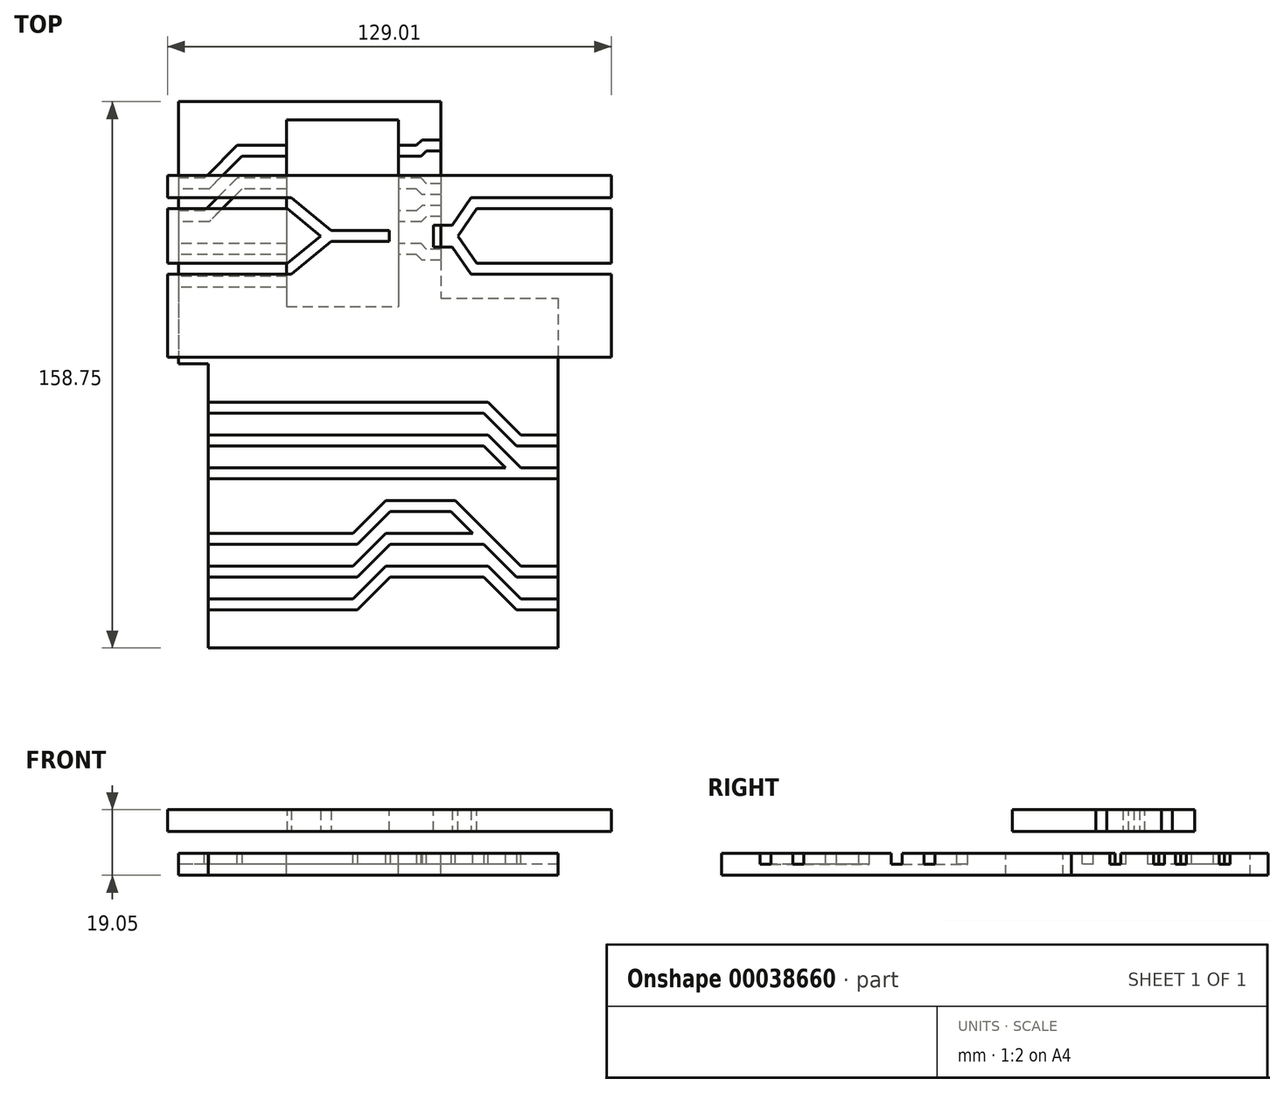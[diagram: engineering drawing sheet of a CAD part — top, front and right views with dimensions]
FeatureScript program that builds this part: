
annotation { "Feature Type Name" : "Feature", "Feature Type Description" : "" }
export const myFeature = defineFeature(function(context is Context, id is Id, definition is map)
    precondition{}
    {
        {
            var Q0;
            Q0=qCreatedBy(makeId("Top.planeOp"),FACE);
            var sketch = newSketch(context, id + "F0", { "sketchPlane" : qUnion([Q0])});
            skLineSegment(sketch, "E0.bottom", {"start": v(-61.1, 34.26) * mm, "end": v(40.5, 34.26) * mm});
            skLineSegment(sketch, "E0.top", {"start": v(-61.1, -67.34) * mm, "end": v(40.5, -67.34) * mm});
            skLineSegment(sketch, "E0.left", {"start": v(-61.1, 34.26) * mm, "end": v(-61.1, -67.34) * mm});
            skLineSegment(sketch, "E0.right", {"start": v(40.5, 34.26) * mm, "end": v(40.5, -67.34) * mm});
            skLineSegment(sketch, "E1.bottom", {"start": v(-69.8, 91.4) * mm, "end": v(6.4, 91.4) * mm});
            skLineSegment(sketch, "E1.top", {"start": v(-69.8, 15.2) * mm, "end": v(6.4, 15.2) * mm});
            skLineSegment(sketch, "E1.left", {"start": v(-69.8, 91.4) * mm, "end": v(-69.8, 15.2) * mm});
            skLineSegment(sketch, "E1.right", {"start": v(6.4, 91.4) * mm, "end": v(6.4, 15.2) * mm});
            skPoint(sketch, "E2", {"position": v(-61.1, 15.2) * mm});
            skPoint(sketch, "E3", {"position": v(6.4, 34.26) * mm});
            skSolve(sketch);
        }
        {
            var Q0;
            {var subQ1=sQuery(id+"F0.wireOp",EDGE,"E0.bottom");var subQ5=sQuery(id+"F0.wireOp",EDGE,"E0.left");var subQ7=makeQuery(id+"F0.imprint","INTERSECT",VERTEX,{"derivedFrom":[subQ1,subQ5]});Q0=makeQuery(id+"F0.imprint","IMPRINT",FACE,{"disambiguationData":[TD([[makeQuery(id+"F0.imprint","IMPRINT",EDGE,{"disambiguationData":[TD([[subQ7,-1.0]])],"derivedFrom":subQ1}),-1.0]])]});}
            var Q1;
            {var subQ8=sQuery(id+"F0.wireOp",EDGE,"E0.top");Q1=makeQuery(id+"F0.imprint","IMPRINT",FACE,{"disambiguationData":[TD([[makeQuery(id+"F0.imprint","IMPRINT",EDGE,{"derivedFrom":subQ8}),1.0]])]});}
            var Q2;
            {var subQ6=sQuery(id+"F0.wireOp",EDGE,"E1.bottom");Q2=makeQuery(id+"F0.imprint","IMPRINT",FACE,{"disambiguationData":[TD([[makeQuery(id+"F0.imprint","IMPRINT",EDGE,{"derivedFrom":subQ6}),-1.0]])]});}
            extrude(context, id + "F1", {"entities" : qUnion([Q0, Q1, Q2]), "oppositeDirection" : true, "depth" : 6.35 * mm});
        }
        {
            var Q0;
            Q0=makeQuery(id+"F1.opExtrude","CAP_FACE",FACE,{"disambiguationData":[OSD([sQuery(id+"F0.wireOp",EDGE,"E0.bottom"),sQuery(id+"F0.wireOp",EDGE,"E0.top"),sQuery(id+"F0.wireOp",EDGE,"E0.left"),sQuery(id+"F0.wireOp",EDGE,"E0.right"),sQuery(id+"F0.wireOp",EDGE,"E1.bottom"),sQuery(id+"F0.wireOp",EDGE,"E1.top"),sQuery(id+"F0.wireOp",EDGE,"E1.left"),sQuery(id+"F0.wireOp",EDGE,"E1.right")])],"isStart":true});
            var sketch = newSketch(context, id + "F2", { "sketchPlane" : qUnion([Q0])});
            skLineSegment(sketch, "E4", {"start": v(40.5, -7.02) * mm, "end": v(29.07, -7.02) * mm});
            skLineSegment(sketch, "E5", {"start": v(29.07, -7.02) * mm, "end": v(19.55, 2.5) * mm});
            skLineSegment(sketch, "E6", {"start": v(19.55, 2.5) * mm, "end": v(-61.1, 2.5) * mm});
            skLineSegment(sketch, "E7", {"start": v(40.5, -16.54) * mm, "end": v(29.07, -16.54) * mm});
            skLineSegment(sketch, "E8", {"start": v(29.07, -16.54) * mm, "end": v(19.55, -7.02) * mm});
            skLineSegment(sketch, "E9", {"start": v(19.55, -7.02) * mm, "end": v(-61.1, -7.02) * mm});
            skLineSegment(sketch, "E10", {"start": v(29.07, -16.54) * mm, "end": v(-61.1, -16.54) * mm});
            skLineSegment(sketch, "E11", {"start": v(40.5, -45.12) * mm, "end": v(29.07, -45.12) * mm});
            skLineSegment(sketch, "E12", {"start": v(29.07, -45.12) * mm, "end": v(19.55, -35.6) * mm});
            skLineSegment(sketch, "E13", {"start": v(10.02, -26.07) * mm, "end": v(-8.92, -26.07) * mm});
            skLineSegment(sketch, "E14", {"start": v(-8.92, -26.07) * mm, "end": v(-18.45, -35.6) * mm});
            skLineSegment(sketch, "E15", {"start": v(-18.45, -35.6) * mm, "end": v(-61.1, -35.6) * mm});
            skLineSegment(sketch, "E16", {"start": v(19.55, -35.6) * mm, "end": v(-8.92, -35.6) * mm});
            skLineSegment(sketch, "E17", {"start": v(-8.92, -35.6) * mm, "end": v(-18.45, -45.12) * mm});
            skLineSegment(sketch, "E18", {"start": v(-18.45, -45.12) * mm, "end": v(-61.1, -45.12) * mm});
            skLineSegment(sketch, "E19", {"start": v(40.5, -54.64) * mm, "end": v(29.07, -54.64) * mm});
            skLineSegment(sketch, "E20", {"start": v(29.07, -54.64) * mm, "end": v(19.55, -45.12) * mm});
            skLineSegment(sketch, "E21", {"start": v(19.55, -45.12) * mm, "end": v(-8.92, -45.12) * mm});
            skLineSegment(sketch, "E22", {"start": v(-8.92, -45.12) * mm, "end": v(-18.45, -54.64) * mm});
            skLineSegment(sketch, "E23", {"start": v(-18.45, -54.64) * mm, "end": v(-61.1, -54.64) * mm});
            skLineSegment(sketch, "E24", {"start": v(40.5, -7.02) * mm, "end": v(40.5, -16.54) * mm, "construction": true});
            skLineSegment(sketch, "E25", {"start": v(40.5, -45.12) * mm, "end": v(40.5, -54.64) * mm});
            skLineSegment(sketch, "E26", {"start": v(-61.1, 2.5) * mm, "end": v(-61.1, -7.02) * mm, "construction": true});
            skLineSegment(sketch, "E27", {"start": v(-61.1, -7.02) * mm, "end": v(-61.1, -16.54) * mm, "construction": true});
            skLineSegment(sketch, "E28", {"start": v(-61.1, -35.6) * mm, "end": v(-61.1, -45.12) * mm, "construction": true});
            skLineSegment(sketch, "E29", {"start": v(-61.1, -45.12) * mm, "end": v(-61.1, -54.64) * mm, "construction": true});
            skLineSegment(sketch, "E30", {"start": v(-4.6, 2.5) * mm, "end": v(-4.6, -7.02) * mm, "construction": true});
            skLineSegment(sketch, "E31", {"start": v(-4.6, -7.02) * mm, "end": v(-4.6, -16.54) * mm, "construction": true});
            skLineSegment(sketch, "E32", {"start": v(-4.92, -26.07) * mm, "end": v(-4.92, -35.6) * mm, "construction": true});
            skLineSegment(sketch, "E33", {"start": v(-4.92, -35.6) * mm, "end": v(-4.92, -45.12) * mm, "construction": true});
            skLineSegment(sketch, "E34", {"start": v(19.55, -35.6) * mm, "end": v(10.02, -26.07) * mm});
            skSolve(sketch);
        }
        {
            var Q0;
            Q0=makeQuery(id+"F1.opExtrude","SWEPT_FACE",FACE,{"disambiguationData":[OSD([sQuery(id+"F0.wireOp",EDGE,"E0.right")])]});
            var sketch = newSketch(context, id + "F3", { "sketchPlane" : qUnion([Q0])});
            skPoint(sketch, "E35.0", {"position": v(-54.64, 0) * mm});
            skPoint(sketch, "E36.0", {"position": v(-45.12, 0) * mm});
            skPoint(sketch, "E37.0", {"position": v(-16.54, 0) * mm});
            skPoint(sketch, "E38.0", {"position": v(-7.02, 0) * mm});
            skLineSegment(sketch, "E39.rect.bottom", {"start": v(-53.05, -3.18) * mm, "end": v(-56.23, -3.18) * mm});
            skLineSegment(sketch, "E39.rect.top", {"start": v(-53.05, 3.18) * mm, "end": v(-56.23, 3.18) * mm});
            skLineSegment(sketch, "E39.rect.left", {"start": v(-53.05, -3.18) * mm, "end": v(-53.05, 3.18) * mm});
            skLineSegment(sketch, "E39.rect.right", {"start": v(-56.23, -3.18) * mm, "end": v(-56.23, 3.18) * mm});
            skLineSegment(sketch, "E40.rect.bottom", {"start": v(-43.53, -3.18) * mm, "end": v(-46.7, -3.18) * mm});
            skLineSegment(sketch, "E40.rect.top", {"start": v(-43.53, 3.17) * mm, "end": v(-46.7, 3.17) * mm});
            skLineSegment(sketch, "E40.rect.left", {"start": v(-43.53, -3.18) * mm, "end": v(-43.53, 3.17) * mm});
            skLineSegment(sketch, "E40.rect.right", {"start": v(-46.7, -3.18) * mm, "end": v(-46.7, 3.17) * mm});
            skLineSegment(sketch, "E41.rect.bottom", {"start": v(-14.95, -3.18) * mm, "end": v(-18.13, -3.18) * mm});
            skLineSegment(sketch, "E41.rect.top", {"start": v(-14.95, 3.17) * mm, "end": v(-18.13, 3.18) * mm});
            skLineSegment(sketch, "E41.rect.left", {"start": v(-14.95, -3.18) * mm, "end": v(-14.95, 3.18) * mm});
            skLineSegment(sketch, "E41.rect.right", {"start": v(-18.13, -3.18) * mm, "end": v(-18.13, 3.18) * mm});
            skLineSegment(sketch, "E42.rect.bottom", {"start": v(-5.43, -3.18) * mm, "end": v(-8.6, -3.18) * mm});
            skLineSegment(sketch, "E42.rect.top", {"start": v(-5.43, 3.18) * mm, "end": v(-8.6, 3.18) * mm});
            skLineSegment(sketch, "E42.rect.left", {"start": v(-5.43, -3.18) * mm, "end": v(-5.43, 3.18) * mm});
            skLineSegment(sketch, "E42.rect.right", {"start": v(-8.6, -3.18) * mm, "end": v(-8.6, 3.18) * mm});
            skLineSegment(sketch, "E43", {"start": v(-67.34, -3.18) * mm, "end": v(34.26, -3.18) * mm, "construction": true});
            skPoint(sketch, "E43.endSnap0", {"position": v(-7.02, -3.18) * mm});
            skSolve(sketch);
        }
        {
            var Q0;
            {var subQ3=sQuery(id+"F3.wireOp",EDGE,"E39.rect.bottom");Q0=makeQuery(id+"F3.imprint","IMPRINT",FACE,{"disambiguationData":[TD([[makeQuery(id+"F3.imprint","IMPRINT",EDGE,{"derivedFrom":subQ3}),-1.0]])]});}
            var Q1;
            Q1=sQuery(id+"F2.wireOp",EDGE,"E19");
            var Q2;
            Q2=sQuery(id+"F2.wireOp",EDGE,"E20");
            var Q3;
            Q3=sQuery(id+"F2.wireOp",EDGE,"E21");
            var Q4;
            Q4=sQuery(id+"F2.wireOp",EDGE,"E22");
            var Q5;
            Q5=sQuery(id+"F2.wireOp",EDGE,"E23");
            sweep(context, id + "F4", {"operationType" : NewBodyOperationType.REMOVE, "profiles" : qUnion([Q0]), "path" : qUnion([Q1, Q2, Q3, Q4, Q5])});
        }
        {
            var Q0;
            {var subQ5=sQuery(id+"F3.wireOp",EDGE,"E40.rect.bottom");Q0=makeQuery(id+"F3.imprint","IMPRINT",FACE,{"disambiguationData":[TD([[makeQuery(id+"F3.imprint","IMPRINT",EDGE,{"derivedFrom":subQ5}),-1.0]])]});}
            var Q1;
            Q1=sQuery(id+"F2.wireOp",EDGE,"E11");
            var Q2;
            Q2=sQuery(id+"F2.wireOp",EDGE,"E12");
            var Q3;
            Q3=sQuery(id+"F2.wireOp",EDGE,"E16");
            var Q4;
            Q4=sQuery(id+"F2.wireOp",EDGE,"E17");
            var Q5;
            Q5=sQuery(id+"F2.wireOp",EDGE,"E18");
            sweep(context, id + "F5", {"operationType" : NewBodyOperationType.REMOVE, "profiles" : qUnion([Q0]), "path" : qUnion([Q1, Q2, Q3, Q4, Q5])});
        }
        {
            var Q0;
            {var subQ5=sQuery(id+"F3.wireOp",EDGE,"E40.rect.bottom");Q0=makeQuery(id+"F3.imprint","IMPRINT",FACE,{"disambiguationData":[TD([[makeQuery(id+"F3.imprint","IMPRINT",EDGE,{"derivedFrom":subQ5}),-1.0]])]});}
            var Q1;
            Q1=sQuery(id+"F2.wireOp",EDGE,"E11");
            var Q2;
            Q2=sQuery(id+"F2.wireOp",EDGE,"E12");
            var Q3;
            Q3=sQuery(id+"F2.wireOp",EDGE,"E34");
            var Q4;
            Q4=sQuery(id+"F2.wireOp",EDGE,"E13");
            var Q5;
            Q5=sQuery(id+"F2.wireOp",EDGE,"E14");
            var Q6;
            Q6=sQuery(id+"F2.wireOp",EDGE,"E15");
            sweep(context, id + "F6", {"operationType" : NewBodyOperationType.REMOVE, "profiles" : qUnion([Q0]), "path" : qUnion([Q1, Q2, Q3, Q4, Q5, Q6])});
        }
        {
            var Q0;
            {var subQ3=sQuery(id+"F3.wireOp",EDGE,"E41.rect.bottom");Q0=makeQuery(id+"F3.imprint","IMPRINT",FACE,{"disambiguationData":[TD([[makeQuery(id+"F3.imprint","IMPRINT",EDGE,{"derivedFrom":subQ3}),-1.0]])]});}
            var Q1;
            Q1=sQuery(id+"F2.wireOp",EDGE,"E7");
            var Q2;
            Q2=sQuery(id+"F2.wireOp",EDGE,"E10");
            sweep(context, id + "F7", {"operationType" : NewBodyOperationType.REMOVE, "profiles" : qUnion([Q0]), "path" : qUnion([Q1, Q2])});
        }
        {
            var Q0;
            {var subQ3=sQuery(id+"F3.wireOp",EDGE,"E41.rect.bottom");Q0=makeQuery(id+"F3.imprint","IMPRINT",FACE,{"disambiguationData":[TD([[makeQuery(id+"F3.imprint","IMPRINT",EDGE,{"derivedFrom":subQ3}),-1.0]])]});}
            var Q1;
            Q1=sQuery(id+"F2.wireOp",EDGE,"E7");
            var Q2;
            Q2=sQuery(id+"F2.wireOp",EDGE,"E8");
            var Q3;
            Q3=sQuery(id+"F2.wireOp",EDGE,"E9");
            sweep(context, id + "F8", {"operationType" : NewBodyOperationType.REMOVE, "profiles" : qUnion([Q0]), "path" : qUnion([Q1, Q2, Q3])});
        }
        {
            var Q0;
            {var subQ3=sQuery(id+"F3.wireOp",EDGE,"E42.rect.bottom");Q0=makeQuery(id+"F3.imprint","IMPRINT",FACE,{"disambiguationData":[TD([[makeQuery(id+"F3.imprint","IMPRINT",EDGE,{"derivedFrom":subQ3}),-1.0]])]});}
            var Q1;
            Q1=sQuery(id+"F2.wireOp",EDGE,"E4");
            var Q2;
            Q2=sQuery(id+"F2.wireOp",EDGE,"E5");
            var Q3;
            Q3=sQuery(id+"F2.wireOp",EDGE,"E6");
            sweep(context, id + "F9", {"operationType" : NewBodyOperationType.REMOVE, "profiles" : qUnion([Q0]), "path" : qUnion([Q1, Q2, Q3])});
        }
        {
            var Q0;
            {var subQ0=sQuery(id+"F0.wireOp",EDGE,"E0.bottom");var subQ1=sQuery(id+"F0.wireOp",EDGE,"E0.left");var subQ2=sQuery(id+"F0.wireOp",EDGE,"E0.right");var subQ3=sQuery(id+"F0.wireOp",EDGE,"E1.bottom");var subQ4=sQuery(id+"F0.wireOp",EDGE,"E1.top");var subQ5=sQuery(id+"F0.wireOp",EDGE,"E1.left");var subQ6=sQuery(id+"F0.wireOp",EDGE,"E1.right");var subQ11=makeQuery(id+"F1.opExtrude","SWEPT_FACE",FACE,{"disambiguationData":[OSD([subQ0])]});Q0=makeQuery(id+"F9.boolean.opBoolean","SPLIT",FACE,{"disambiguationData":[TD([subQ11])],"derivedFrom":makeQuery(id+"F8.boolean.opBoolean","SPLIT",FACE,{"disambiguationData":[TD([subQ11])],"derivedFrom":makeQuery(id+"F7.boolean.opBoolean","SPLIT",FACE,{"disambiguationData":[TD([subQ11])],"derivedFrom":makeQuery(id+"F6.boolean.opBoolean","SPLIT",FACE,{"disambiguationData":[TD([subQ11])],"derivedFrom":makeQuery(id+"F5.boolean.opBoolean","SPLIT",FACE,{"disambiguationData":[TD([subQ11])],"derivedFrom":makeQuery(id+"F4.boolean.opBoolean","SPLIT",FACE,{"disambiguationData":[TD([subQ11])],"derivedFrom":makeQuery(id+"F1.opExtrude","CAP_FACE",FACE,{"disambiguationData":[OSD([subQ0,sQuery(id+"F0.wireOp",EDGE,"E0.top"),subQ1,subQ2,subQ3,subQ4,subQ5,subQ6])],"isStart":true})})})})})})});}
            var sketch = newSketch(context, id + "F10", { "sketchPlane" : qUnion([Q0])});
            skLineSegment(sketch, "E44", {"start": v(6.4, 78.72) * mm, "end": v(1.59, 78.72) * mm});
            skLineSegment(sketch, "E45", {"start": v(1.59, 78.72) * mm, "end": v(0, 77.14) * mm});
            skLineSegment(sketch, "E46", {"start": v(0, 77.14) * mm, "end": v(-5.83, 77.14) * mm});
            skLineSegment(sketch, "E47", {"start": v(6.4, 66.02) * mm, "end": v(1.59, 66.02) * mm});
            skLineSegment(sketch, "E48", {"start": v(1.59, 66.02) * mm, "end": v(0, 67.61) * mm});
            skLineSegment(sketch, "E49", {"start": v(0, 67.61) * mm, "end": v(-5.83, 67.61) * mm});
            skLineSegment(sketch, "E50", {"start": v(6.4, 59.67) * mm, "end": v(1.59, 59.67) * mm});
            skLineSegment(sketch, "E51", {"start": v(1.59, 59.67) * mm, "end": v(0, 58.09) * mm});
            skLineSegment(sketch, "E52", {"start": v(0, 58.09) * mm, "end": v(-5.83, 58.09) * mm});
            skLineSegment(sketch, "E53", {"start": v(6.4, 46.97) * mm, "end": v(1.59, 46.97) * mm});
            skLineSegment(sketch, "E54", {"start": v(1.59, 46.97) * mm, "end": v(0, 48.56) * mm});
            skLineSegment(sketch, "E55", {"start": v(0, 48.56) * mm, "end": v(-5.83, 48.56) * mm});
            skLineSegment(sketch, "E56", {"start": v(-69.8, 67.61) * mm, "end": v(-61.6, 67.61) * mm});
            skLineSegment(sketch, "E57", {"start": v(-61.6, 67.61) * mm, "end": v(-52.08, 77.14) * mm});
            skLineSegment(sketch, "E58", {"start": v(-52.08, 77.14) * mm, "end": v(-38.37, 77.14) * mm});
            skLineSegment(sketch, "E59", {"start": v(-69.8, 58.09) * mm, "end": v(-61.6, 58.09) * mm});
            skLineSegment(sketch, "E60", {"start": v(-61.6, 58.09) * mm, "end": v(-52.08, 67.61) * mm});
            skLineSegment(sketch, "E61", {"start": v(-52.08, 67.61) * mm, "end": v(-38.37, 67.61) * mm});
            skLineSegment(sketch, "E62", {"start": v(-69.8, 48.56) * mm, "end": v(-38.37, 48.56) * mm});
            skLineSegment(sketch, "E63", {"start": v(-69.8, 39.04) * mm, "end": v(-38.37, 39.04) * mm});
            skLineSegment(sketch, "E64", {"start": v(-69.8, 67.61) * mm, "end": v(-69.8, 58.09) * mm, "construction": true});
            skLineSegment(sketch, "E65", {"start": v(-69.8, 58.09) * mm, "end": v(-69.8, 48.56) * mm, "construction": true});
            skLineSegment(sketch, "E66", {"start": v(-69.8, 48.56) * mm, "end": v(-69.8, 39.04) * mm, "construction": true});
            skLineSegment(sketch, "E67", {"start": v(-61.1, 15.2) * mm, "end": v(-61.1, 91.4) * mm, "construction": true});
            skLineSegment(sketch, "E68", {"start": v(-5.83, 77.14) * mm, "end": v(-5.83, 67.61) * mm, "construction": true});
            skLineSegment(sketch, "E69", {"start": v(-5.83, 67.61) * mm, "end": v(-5.83, 58.09) * mm, "construction": true});
            skLineSegment(sketch, "E70", {"start": v(-5.83, 58.09) * mm, "end": v(-5.83, 48.56) * mm, "construction": true});
            skLineSegment(sketch, "E71.bottom", {"start": v(-38.37, 86.17) * mm, "end": v(-5.83, 86.17) * mm});
            skLineSegment(sketch, "E71.top", {"start": v(-38.37, 31.86) * mm, "end": v(-5.83, 31.86) * mm});
            skLineSegment(sketch, "E71.left", {"start": v(-38.37, 86.17) * mm, "end": v(-38.37, 31.86) * mm});
            skLineSegment(sketch, "E71.right", {"start": v(-5.83, 86.17) * mm, "end": v(-5.83, 31.86) * mm});
            skSolve(sketch);
        }
        {
            var Q0;
            Q0 = qSketchRegion(id + "F10", true);
            extrude(context, id + "F11", {"entities" : qUnion([Q0]), "operationType" : NewBodyOperationType.REMOVE, "endBound" : BoundingType.THROUGH_ALL, "oppositeDirection" : true, "depth" : 25.4 * mm});
        }
        {
            var Q0;
            Q0=makeQuery(id+"F1.opExtrude","SWEPT_FACE",FACE,{"disambiguationData":[OSD([sQuery(id+"F0.wireOp",EDGE,"E1.right")])]});
            var sketch = newSketch(context, id + "F12", { "sketchPlane" : qUnion([Q0])});
            skPoint(sketch, "E72.0", {"position": v(46.97, 0) * mm});
            skPoint(sketch, "E73.0", {"position": v(59.67, 0) * mm});
            skPoint(sketch, "E74.0", {"position": v(66.02, 0) * mm});
            skPoint(sketch, "E75.0", {"position": v(78.72, 0) * mm});
            skLineSegment(sketch, "E76.rect.bottom", {"start": v(48.56, -3.18) * mm, "end": v(45.39, -3.18) * mm});
            skLineSegment(sketch, "E76.rect.top", {"start": v(48.56, 3.18) * mm, "end": v(45.39, 3.18) * mm});
            skLineSegment(sketch, "E76.rect.left", {"start": v(48.56, -3.18) * mm, "end": v(48.56, 3.18) * mm});
            skLineSegment(sketch, "E76.rect.right", {"start": v(45.39, -3.18) * mm, "end": v(45.39, 3.18) * mm});
            skLineSegment(sketch, "E77.rect.bottom", {"start": v(61.26, -3.18) * mm, "end": v(58.09, -3.18) * mm});
            skLineSegment(sketch, "E77.rect.top", {"start": v(61.26, 3.18) * mm, "end": v(58.09, 3.18) * mm});
            skLineSegment(sketch, "E77.rect.left", {"start": v(61.26, -3.18) * mm, "end": v(61.26, 3.18) * mm});
            skLineSegment(sketch, "E77.rect.right", {"start": v(58.09, -3.18) * mm, "end": v(58.09, 3.18) * mm});
            skLineSegment(sketch, "E78.rect.bottom", {"start": v(67.61, -3.18) * mm, "end": v(64.44, -3.18) * mm});
            skLineSegment(sketch, "E78.rect.top", {"start": v(67.61, 3.18) * mm, "end": v(64.44, 3.18) * mm});
            skLineSegment(sketch, "E78.rect.left", {"start": v(67.61, -3.18) * mm, "end": v(67.61, 3.18) * mm});
            skLineSegment(sketch, "E78.rect.right", {"start": v(64.44, -3.18) * mm, "end": v(64.44, 3.18) * mm});
            skLineSegment(sketch, "E79.rect.bottom", {"start": v(80.31, -3.18) * mm, "end": v(77.14, -3.18) * mm});
            skLineSegment(sketch, "E79.rect.top", {"start": v(80.31, 3.18) * mm, "end": v(77.14, 3.18) * mm});
            skLineSegment(sketch, "E79.rect.left", {"start": v(80.31, -3.18) * mm, "end": v(80.31, 3.18) * mm});
            skLineSegment(sketch, "E79.rect.right", {"start": v(77.14, -3.18) * mm, "end": v(77.14, 3.18) * mm});
            skLineSegment(sketch, "E80", {"start": v(91.4, -3.18) * mm, "end": v(34.26, -3.18) * mm});
            skSolve(sketch);
        }
        {
            var Q0;
            {var subQ3=sQuery(id+"F12.wireOp",EDGE,"E76.rect.left");var subQ5=sQuery(id+"F12.wireOp",EDGE,"E80");var subQ7=makeQuery(id+"F12.imprint","INTERSECT",VERTEX,{"derivedFrom":[subQ3,subQ5]});Q0=makeQuery(id+"F12.imprint","IMPRINT",FACE,{"disambiguationData":[TD([[makeQuery(id+"F12.imprint","IMPRINT",EDGE,{"disambiguationData":[TD([[subQ7,-1.0]])],"derivedFrom":subQ3}),1.0]])]});}
            var Q1;
            Q1=sQuery(id+"F10.wireOp",EDGE,"E53");
            var Q2;
            Q2=sQuery(id+"F10.wireOp",EDGE,"E54");
            var Q3;
            Q3=sQuery(id+"F10.wireOp",EDGE,"E55");
            sweep(context, id + "F13", {"operationType" : NewBodyOperationType.REMOVE, "profiles" : qUnion([Q0]), "path" : qUnion([Q1, Q2, Q3])});
        }
        {
            var Q0;
            {var subQ0=sQuery(id+"F12.wireOp",EDGE,"E80");var subQ3=sQuery(id+"F12.wireOp",EDGE,"E77.rect.left");var subQ4=makeQuery(id+"F12.imprint","INTERSECT",VERTEX,{"derivedFrom":[subQ3,subQ0]});Q0=makeQuery(id+"F12.imprint","IMPRINT",FACE,{"disambiguationData":[TD([[makeQuery(id+"F12.imprint","IMPRINT",EDGE,{"disambiguationData":[TD([[subQ4,-1.0]])],"derivedFrom":subQ3}),1.0]])]});}
            var Q1;
            Q1=sQuery(id+"F10.wireOp",EDGE,"E50");
            var Q2;
            Q2=sQuery(id+"F10.wireOp",EDGE,"E51");
            var Q3;
            Q3=sQuery(id+"F10.wireOp",EDGE,"E52");
            sweep(context, id + "F14", {"operationType" : NewBodyOperationType.REMOVE, "profiles" : qUnion([Q0]), "path" : qUnion([Q1, Q2, Q3])});
        }
        {
            var Q0;
            {var subQ0=sQuery(id+"F12.wireOp",EDGE,"E80");var subQ3=sQuery(id+"F12.wireOp",EDGE,"E78.rect.left");var subQ4=makeQuery(id+"F12.imprint","INTERSECT",VERTEX,{"derivedFrom":[subQ3,subQ0]});Q0=makeQuery(id+"F12.imprint","IMPRINT",FACE,{"disambiguationData":[TD([[makeQuery(id+"F12.imprint","IMPRINT",EDGE,{"disambiguationData":[TD([[subQ4,-1.0]])],"derivedFrom":subQ3}),1.0]])]});}
            var Q1;
            Q1=sQuery(id+"F10.wireOp",EDGE,"E47");
            var Q2;
            Q2=sQuery(id+"F10.wireOp",EDGE,"E48");
            var Q3;
            Q3=sQuery(id+"F10.wireOp",EDGE,"E49");
            sweep(context, id + "F15", {"operationType" : NewBodyOperationType.REMOVE, "profiles" : qUnion([Q0]), "path" : qUnion([Q1, Q2, Q3])});
        }
        {
            var Q0;
            {var subQ3=sQuery(id+"F12.wireOp",EDGE,"E79.rect.left");var subQ5=sQuery(id+"F12.wireOp",EDGE,"E80");var subQ7=makeQuery(id+"F12.imprint","INTERSECT",VERTEX,{"derivedFrom":[subQ3,subQ5]});Q0=makeQuery(id+"F12.imprint","IMPRINT",FACE,{"disambiguationData":[TD([[makeQuery(id+"F12.imprint","IMPRINT",EDGE,{"disambiguationData":[TD([[subQ7,-1.0]])],"derivedFrom":subQ3}),1.0]])]});}
            var Q1;
            Q1=sQuery(id+"F10.wireOp",EDGE,"E44");
            var Q2;
            Q2=sQuery(id+"F10.wireOp",EDGE,"E45");
            var Q3;
            Q3=sQuery(id+"F10.wireOp",EDGE,"E46");
            sweep(context, id + "F16", {"operationType" : NewBodyOperationType.REMOVE, "profiles" : qUnion([Q0]), "path" : qUnion([Q1, Q2, Q3])});
        }
        {
            var Q0;
            Q0=makeQuery(id+"F11.boolean.opBoolean","COPY",FACE,{"derivedFrom":makeQuery(id+"F11.opExtrude","SWEPT_FACE",FACE,{"disambiguationData":[OSD([sQuery(id+"F10.wireOp",EDGE,"E71.left")])]})});
            var sketch = newSketch(context, id + "F17", { "sketchPlane" : qUnion([Q0])});
            skPoint(sketch, "E81.0", {"position": v(39.04, 0) * mm});
            skPoint(sketch, "E82.0", {"position": v(48.56, 0) * mm});
            skPoint(sketch, "E83.0", {"position": v(67.61, 0) * mm});
            skPoint(sketch, "E84.0", {"position": v(77.14, 0) * mm});
            skLineSegment(sketch, "E85.rect.bottom", {"start": v(40.62, -3.17) * mm, "end": v(37.45, -3.17) * mm});
            skLineSegment(sketch, "E85.rect.top", {"start": v(40.62, 3.17) * mm, "end": v(37.45, 3.17) * mm});
            skLineSegment(sketch, "E85.rect.left", {"start": v(40.62, -3.18) * mm, "end": v(40.62, 3.18) * mm});
            skLineSegment(sketch, "E85.rect.right", {"start": v(37.45, -3.18) * mm, "end": v(37.45, 3.18) * mm});
            skLineSegment(sketch, "E86.rect.bottom", {"start": v(50.15, -3.18) * mm, "end": v(46.97, -3.18) * mm});
            skLineSegment(sketch, "E86.rect.top", {"start": v(50.15, 3.18) * mm, "end": v(46.97, 3.18) * mm});
            skLineSegment(sketch, "E86.rect.left", {"start": v(50.15, -3.18) * mm, "end": v(50.15, 3.18) * mm});
            skLineSegment(sketch, "E86.rect.right", {"start": v(46.97, -3.18) * mm, "end": v(46.97, 3.18) * mm});
            skLineSegment(sketch, "E87.rect.bottom", {"start": v(69.2, -3.18) * mm, "end": v(66.02, -3.18) * mm});
            skLineSegment(sketch, "E87.rect.top", {"start": v(69.2, 3.18) * mm, "end": v(66.02, 3.18) * mm});
            skLineSegment(sketch, "E87.rect.left", {"start": v(69.2, -3.18) * mm, "end": v(69.2, 3.18) * mm});
            skLineSegment(sketch, "E87.rect.right", {"start": v(66.02, -3.18) * mm, "end": v(66.02, 3.18) * mm});
            skLineSegment(sketch, "E88.rect.bottom", {"start": v(78.72, -3.18) * mm, "end": v(75.55, -3.18) * mm});
            skLineSegment(sketch, "E88.rect.top", {"start": v(78.72, 3.18) * mm, "end": v(75.55, 3.18) * mm});
            skLineSegment(sketch, "E88.rect.left", {"start": v(78.72, -3.18) * mm, "end": v(78.72, 3.18) * mm});
            skLineSegment(sketch, "E88.rect.right", {"start": v(75.55, -3.18) * mm, "end": v(75.55, 3.18) * mm});
            skLineSegment(sketch, "E89", {"start": v(35.43, -3.18) * mm, "end": v(86.17, -3.18) * mm, "construction": true});
            skPoint(sketch, "E89.startSnap0", {"position": v(31.86, -3.18) * mm});
            skSolve(sketch);
        }
        {
            var Q0;
            {var subQ3=sQuery(id+"F17.wireOp",EDGE,"E85.rect.bottom");Q0=makeQuery(id+"F17.imprint","IMPRINT",FACE,{"disambiguationData":[TD([[makeQuery(id+"F17.imprint","IMPRINT",EDGE,{"derivedFrom":subQ3}),-1.0]])]});}
            var Q1;
            Q1=sQuery(id+"F10.wireOp",EDGE,"E63");
            sweep(context, id + "F18", {"operationType" : NewBodyOperationType.REMOVE, "profiles" : qUnion([Q0]), "path" : qUnion([Q1])});
        }
        {
            var Q0;
            {var subQ3=sQuery(id+"F17.wireOp",EDGE,"E86.rect.bottom");Q0=makeQuery(id+"F17.imprint","IMPRINT",FACE,{"disambiguationData":[TD([[makeQuery(id+"F17.imprint","IMPRINT",EDGE,{"derivedFrom":subQ3}),-1.0]])]});}
            var Q1;
            Q1=sQuery(id+"F10.wireOp",EDGE,"E62");
            sweep(context, id + "F19", {"operationType" : NewBodyOperationType.REMOVE, "profiles" : qUnion([Q0]), "path" : qUnion([Q1])});
        }
        {
            var Q0;
            {var subQ5=sQuery(id+"F17.wireOp",EDGE,"E87.rect.bottom");Q0=makeQuery(id+"F17.imprint","IMPRINT",FACE,{"disambiguationData":[TD([[makeQuery(id+"F17.imprint","IMPRINT",EDGE,{"derivedFrom":subQ5}),-1.0]])]});}
            var Q1;
            Q1=sQuery(id+"F10.wireOp",EDGE,"E61");
            var Q2;
            Q2=sQuery(id+"F10.wireOp",EDGE,"E60");
            var Q3;
            Q3=sQuery(id+"F10.wireOp",EDGE,"E59");
            sweep(context, id + "F20", {"operationType" : NewBodyOperationType.REMOVE, "profiles" : qUnion([Q0]), "path" : qUnion([Q1, Q2, Q3])});
        }
        {
            var Q0;
            {var subQ3=sQuery(id+"F17.wireOp",EDGE,"E88.rect.bottom");Q0=makeQuery(id+"F17.imprint","IMPRINT",FACE,{"disambiguationData":[TD([[makeQuery(id+"F17.imprint","IMPRINT",EDGE,{"derivedFrom":subQ3}),-1.0]])]});}
            var Q1;
            Q1=sQuery(id+"F10.wireOp",EDGE,"E58");
            var Q2;
            Q2=sQuery(id+"F10.wireOp",EDGE,"E57");
            var Q3;
            Q3=sQuery(id+"F10.wireOp",EDGE,"E56");
            sweep(context, id + "F21", {"operationType" : NewBodyOperationType.REMOVE, "profiles" : qUnion([Q0]), "path" : qUnion([Q1, Q2, Q3])});
        }
        {
            var Q0;
            Q0=qCreatedBy(makeId("Top.planeOp"),FACE);
            cPlane(context, id + "F22", {"entities" : qUnion([Q0]), "cplaneType" : CPlaneType.OFFSET, "offset" : 12.7 * mm, "width" : 152.4 * mm, "height" : 152.4 * mm});
        }
        {
            var Q0;
            Q0=qCreatedBy(id+"F22.planeOp",FACE);
            var sketch = newSketch(context, id + "F23", { "sketchPlane" : qUnion([Q0])});
            skLineSegment(sketch, "E90.bottom", {"start": v(-73, 70.05) * mm, "end": v(56.01, 70.05) * mm});
            skLineSegment(sketch, "E90.top", {"start": v(-73, 17.11) * mm, "end": v(56.01, 17.11) * mm});
            skLineSegment(sketch, "E90.left", {"start": v(-73, 70.05) * mm, "end": v(-73, 17.11) * mm});
            skLineSegment(sketch, "E90.right", {"start": v(56.01, 70.05) * mm, "end": v(56.01, 17.11) * mm});
            skSolve(sketch);
        }
        {
            var Q0;
            Q0 = qSketchRegion(id + "F23", true);
            extrude(context, id + "F24", {"entities" : qUnion([Q0]), "oppositeDirection" : true, "depth" : 6.35 * mm});
        }
        {
            var Q0;
            Q0=makeQuery(id+"F24.opExtrude","CAP_FACE",FACE,{"disambiguationData":[OSD([sQuery(id+"F23.wireOp",EDGE,"E90.bottom"),sQuery(id+"F23.wireOp",EDGE,"E90.top"),sQuery(id+"F23.wireOp",EDGE,"E90.left"),sQuery(id+"F23.wireOp",EDGE,"E90.right")])],"isStart":true});
            var sketch = newSketch(context, id + "F25", { "sketchPlane" : qUnion([Q0])});
            skLineSegment(sketch, "E91", {"start": v(-73, 61.9) * mm, "end": v(-37.55, 61.9) * mm});
            skLineSegment(sketch, "E92", {"start": v(-37.55, 61.9) * mm, "end": v(-26.03, 52.38) * mm});
            skLineSegment(sketch, "E93", {"start": v(-26.03, 52.38) * mm, "end": v(-8.5, 52.38) * mm});
            skLineSegment(sketch, "E94", {"start": v(-73, 42.86) * mm, "end": v(-37.55, 42.86) * mm});
            skLineSegment(sketch, "E95", {"start": v(-37.55, 42.86) * mm, "end": v(-26.03, 52.38) * mm});
            skLineSegment(sketch, "E96", {"start": v(56.01, 61.9) * mm, "end": v(16, 61.9) * mm});
            skLineSegment(sketch, "E97", {"start": v(16, 61.9) * mm, "end": v(10.51, 53.97) * mm});
            skLineSegment(sketch, "E98", {"start": v(10.51, 53.97) * mm, "end": v(4.23, 53.97) * mm});
            skLineSegment(sketch, "E99", {"start": v(56.01, 42.86) * mm, "end": v(16, 42.86) * mm});
            skLineSegment(sketch, "E100", {"start": v(16, 42.86) * mm, "end": v(10.51, 50.8) * mm});
            skLineSegment(sketch, "E101", {"start": v(10.51, 50.8) * mm, "end": v(4.23, 50.8) * mm});
            skSolve(sketch);
        }
        {
            var Q0;
            Q0=makeQuery(id+"F24.opExtrude","SWEPT_FACE",FACE,{"disambiguationData":[OSD([sQuery(id+"F23.wireOp",EDGE,"E90.right")])]});
            var sketch = newSketch(context, id + "F26", { "sketchPlane" : qUnion([Q0])});
            skPoint(sketch, "E102.0", {"position": v(42.86, 12.7) * mm});
            skPoint(sketch, "E103.0", {"position": v(61.9, 12.7) * mm});
            skLineSegment(sketch, "E104.rect.bottom", {"start": v(44.44, 5.4) * mm, "end": v(41.27, 5.4) * mm});
            skLineSegment(sketch, "E104.rect.top", {"start": v(44.44, 20) * mm, "end": v(41.27, 20) * mm});
            skLineSegment(sketch, "E104.rect.left", {"start": v(44.44, 5.4) * mm, "end": v(44.44, 20) * mm});
            skLineSegment(sketch, "E104.rect.right", {"start": v(41.27, 5.4) * mm, "end": v(41.27, 20) * mm});
            skLineSegment(sketch, "E105.rect.bottom", {"start": v(60.32, 5.4) * mm, "end": v(63.5, 5.4) * mm});
            skLineSegment(sketch, "E105.rect.top", {"start": v(60.32, 20) * mm, "end": v(63.5, 20) * mm});
            skLineSegment(sketch, "E105.rect.left", {"start": v(60.32, 5.4) * mm, "end": v(60.32, 20) * mm});
            skLineSegment(sketch, "E105.rect.right", {"start": v(63.5, 5.4) * mm, "end": v(63.5, 20) * mm});
            skSolve(sketch);
        }
        {
            var Q0;
            {var subQ0=sQuery(id+"F23.wireOp",EDGE,"E90.right");var subQ1=makeQuery(id+"F24.opExtrude","CAP_EDGE",EDGE,{"disambiguationData":[OSD([subQ0])],"isStart":false});var subQ4=sQuery(id+"F26.wireOp",EDGE,"E104.rect.left");var subQ5=makeQuery(id+"F26.imprint","INTERSECT",VERTEX,{"derivedFrom":[subQ1,subQ4]});Q0=makeQuery(id+"F26.imprint","IMPRINT",FACE,{"disambiguationData":[TD([[makeQuery(id+"F26.imprint","IMPRINT",EDGE,{"disambiguationData":[TD([[subQ5,-1.0]])],"derivedFrom":subQ4}),1.0]])]});}
            var Q1;
            Q1=sQuery(id+"F25.wireOp",EDGE,"E99");
            var Q2;
            Q2=sQuery(id+"F25.wireOp",EDGE,"E100");
            var Q3;
            Q3=sQuery(id+"F25.wireOp",EDGE,"E101");
            sweep(context, id + "F27", {"operationType" : NewBodyOperationType.REMOVE, "profiles" : qUnion([Q0]), "path" : qUnion([Q1, Q2, Q3])});
        }
        {
            var Q0;
            {var subQ0=sQuery(id+"F23.wireOp",EDGE,"E90.right");var subQ1=makeQuery(id+"F24.opExtrude","CAP_EDGE",EDGE,{"disambiguationData":[OSD([subQ0])],"isStart":false});var subQ4=sQuery(id+"F26.wireOp",EDGE,"E105.rect.left");var subQ5=makeQuery(id+"F26.imprint","INTERSECT",VERTEX,{"derivedFrom":[subQ1,subQ4]});Q0=makeQuery(id+"F26.imprint","IMPRINT",FACE,{"disambiguationData":[TD([[makeQuery(id+"F26.imprint","IMPRINT",EDGE,{"disambiguationData":[TD([[subQ5,-1.0]])],"derivedFrom":subQ4}),-1.0]])]});}
            var Q1;
            Q1=sQuery(id+"F25.wireOp",EDGE,"E96");
            var Q2;
            Q2=sQuery(id+"F25.wireOp",EDGE,"E97");
            var Q3;
            Q3=sQuery(id+"F25.wireOp",EDGE,"E98");
            sweep(context, id + "F28", {"operationType" : NewBodyOperationType.REMOVE, "profiles" : qUnion([Q0]), "path" : qUnion([Q1, Q2, Q3])});
        }
        {
            var Q0;
            Q0=makeQuery(id+"F24.opExtrude","SWEPT_FACE",FACE,{"disambiguationData":[OSD([sQuery(id+"F23.wireOp",EDGE,"E90.left")])]});
            var sketch = newSketch(context, id + "F29", { "sketchPlane" : qUnion([Q0])});
            skPoint(sketch, "E106.0", {"position": v(-61.9, 12.7) * mm});
            skPoint(sketch, "E107.0", {"position": v(-42.86, 12.7) * mm});
            skLineSegment(sketch, "E108.rect.bottom", {"start": v(-60.32, 5.47) * mm, "end": v(-63.5, 5.47) * mm});
            skLineSegment(sketch, "E108.rect.top", {"start": v(-60.32, 19.93) * mm, "end": v(-63.5, 19.93) * mm});
            skLineSegment(sketch, "E108.rect.left", {"start": v(-60.32, 5.47) * mm, "end": v(-60.32, 19.93) * mm});
            skLineSegment(sketch, "E108.rect.right", {"start": v(-63.5, 5.47) * mm, "end": v(-63.5, 19.93) * mm});
            skLineSegment(sketch, "E109.rect.bottom", {"start": v(-41.27, 5.5) * mm, "end": v(-44.44, 5.5) * mm});
            skLineSegment(sketch, "E109.rect.top", {"start": v(-41.27, 19.9) * mm, "end": v(-44.44, 19.9) * mm});
            skLineSegment(sketch, "E109.rect.left", {"start": v(-41.27, 5.5) * mm, "end": v(-41.27, 19.9) * mm});
            skLineSegment(sketch, "E109.rect.right", {"start": v(-44.44, 5.5) * mm, "end": v(-44.44, 19.9) * mm});
            skSolve(sketch);
        }
        {
            var Q0;
            {var subQ0=sQuery(id+"F23.wireOp",EDGE,"E90.left");var subQ1=makeQuery(id+"F24.opExtrude","CAP_EDGE",EDGE,{"disambiguationData":[OSD([subQ0])],"isStart":false});var subQ4=sQuery(id+"F29.wireOp",EDGE,"E108.rect.left");var subQ5=makeQuery(id+"F29.imprint","INTERSECT",VERTEX,{"derivedFrom":[subQ1,subQ4]});Q0=makeQuery(id+"F29.imprint","IMPRINT",FACE,{"disambiguationData":[TD([[makeQuery(id+"F29.imprint","IMPRINT",EDGE,{"disambiguationData":[TD([[subQ5,-1.0]])],"derivedFrom":subQ4}),1.0]])]});}
            var Q1;
            Q1=sQuery(id+"F25.wireOp",EDGE,"E91");
            var Q2;
            Q2=sQuery(id+"F25.wireOp",EDGE,"E92");
            var Q3;
            Q3=sQuery(id+"F25.wireOp",EDGE,"E93");
            sweep(context, id + "F30", {"operationType" : NewBodyOperationType.REMOVE, "profiles" : qUnion([Q0]), "path" : qUnion([Q1, Q2, Q3])});
        }
        {
            var Q0;
            {var subQ0=sQuery(id+"F23.wireOp",EDGE,"E90.left");var subQ1=makeQuery(id+"F24.opExtrude","CAP_EDGE",EDGE,{"disambiguationData":[OSD([subQ0])],"isStart":false});var subQ4=sQuery(id+"F29.wireOp",EDGE,"E109.rect.left");var subQ5=makeQuery(id+"F29.imprint","INTERSECT",VERTEX,{"derivedFrom":[subQ1,subQ4]});Q0=makeQuery(id+"F29.imprint","IMPRINT",FACE,{"disambiguationData":[TD([[makeQuery(id+"F29.imprint","IMPRINT",EDGE,{"disambiguationData":[TD([[subQ5,-1.0]])],"derivedFrom":subQ4}),1.0]])]});}
            var Q1;
            Q1=sQuery(id+"F25.wireOp",EDGE,"E94");
            var Q2;
            Q2=sQuery(id+"F25.wireOp",EDGE,"E95");
            sweep(context, id + "F31", {"operationType" : NewBodyOperationType.REMOVE, "profiles" : qUnion([Q0]), "path" : qUnion([Q1, Q2])});
        }
    });
